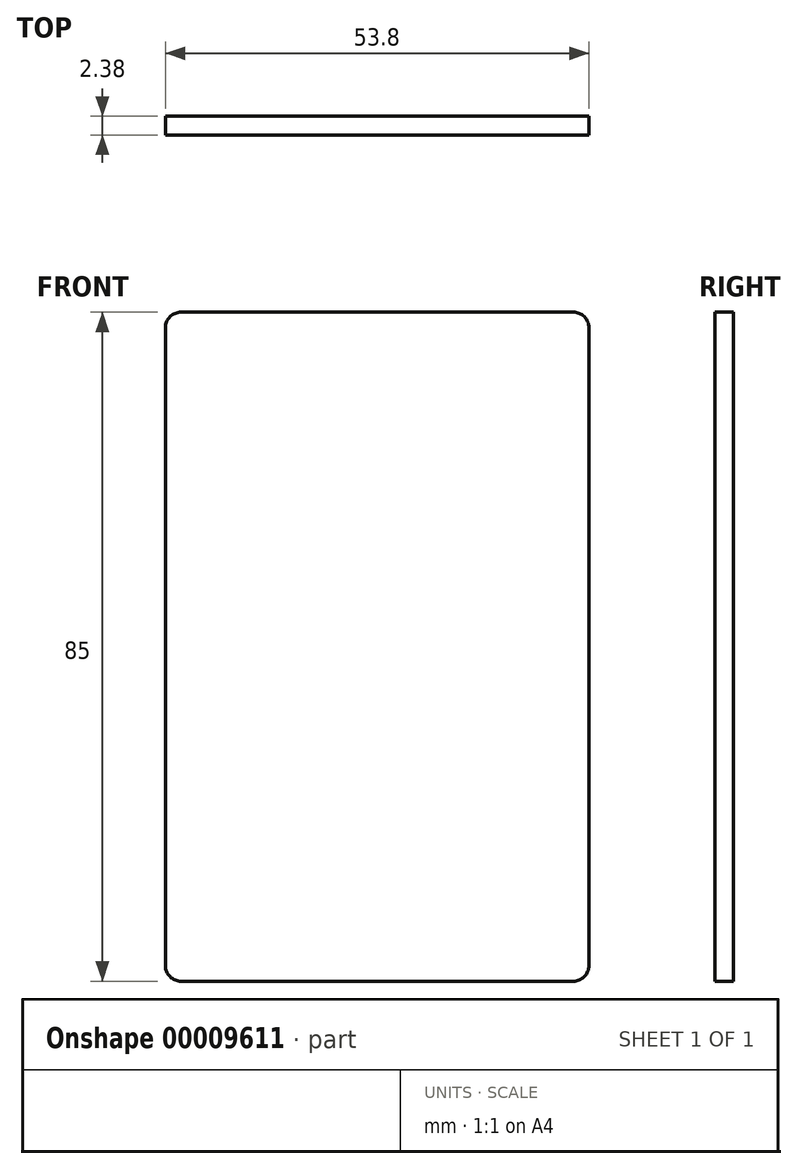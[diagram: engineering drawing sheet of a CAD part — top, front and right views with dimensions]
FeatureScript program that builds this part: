
annotation { "Feature Type Name" : "Feature", "Feature Type Description" : "" }
export const myFeature = defineFeature(function(context is Context, id is Id, definition is map)
    precondition{}
    {
        {
            var Q0;
            Q0=qCreatedBy(makeId("Front.planeOp"),FACE);
            var sketch = newSketch(context, id + "F0", { "sketchPlane" : qUnion([Q0])});
            skLineSegment(sketch, "E0.bottom", {"start": v(-25.05, -39.18) * mm, "end": v(24.75, -39.18) * mm});
            skLineSegment(sketch, "E0.top", {"start": v(-25.05, 45.82) * mm, "end": v(24.75, 45.82) * mm});
            skLineSegment(sketch, "E0.left", {"start": v(-27.05, -37.18) * mm, "end": v(-27.05, 43.82) * mm});
            skLineSegment(sketch, "E0.right", {"start": v(26.75, -37.18) * mm, "end": v(26.75, 43.82) * mm});
            skPoint(sketch, "E1.visualSharp", {"position": v(-27.05, 45.82) * mm});
            skArc(sketch, "E1.filletArc", {"start": v(-25.05, 45.82) * mm, "mid": v(-26.46, 45.23) * mm, "end": v(-27.05, 43.82) * mm});
            skPoint(sketch, "E2.visualSharp", {"position": v(26.75, 45.82) * mm});
            skArc(sketch, "E2.filletArc", {"start": v(26.75, 43.82) * mm, "mid": v(26.17, 45.23) * mm, "end": v(24.75, 45.82) * mm});
            skPoint(sketch, "E3.visualSharp", {"position": v(26.75, -39.18) * mm});
            skArc(sketch, "E3.filletArc", {"start": v(24.75, -39.18) * mm, "mid": v(26.17, -38.6) * mm, "end": v(26.75, -37.18) * mm});
            skPoint(sketch, "E4.visualSharp", {"position": v(-27.05, -39.18) * mm});
            skArc(sketch, "E4.filletArc", {"start": v(-27.05, -37.18) * mm, "mid": v(-26.46, -38.6) * mm, "end": v(-25.05, -39.18) * mm});
            skSolve(sketch);
        }
        {
            var Q0;
            Q0 = qSketchRegion(id + "F0", true);
            extrude(context, id + "F1", {"entities" : qUnion([Q0]), "depth" : 2.38 * mm});
        }
    });
